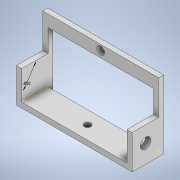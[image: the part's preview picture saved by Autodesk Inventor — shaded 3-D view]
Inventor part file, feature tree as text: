
AUTODESK INVENTOR PART (.ipt)
format: ipt  version: 2021.2 (Build 252289000, 289)  size: 291,328 bytes
history: native  units: in
note: dims shown in document units (in); Inventor stores cm internally (conversion verified against a paired STEP export)
features: sketch x28, extrude x21
ambient origin geometry x8: Origin, YZ Plane, XZ Plane, XY Plane, X Axis, Y Axis, Z Axis, Center Point
bodies: Solid1 (feature_tree)
feature tree (49):
  extrude  "Extrusion1"  Depth=4.0in
  extrude  "Extrusion2"  Depth=0.2in
  sketch  "Sketch3"  dims[d4=0.2in d5=0.2in]
  extrude  "Extrusion3"  Depth=0.2in
  extrude  "Extrusion4"  Depth=2.0in
  sketch  "Sketch7"  dims[d11=0.1875in d12=0.0in d13=0.125in d14=0.0in]
  extrude  "Extrusion6"  Depth=0.2in
  sketch  "Sketch9"  dims[d21=0.3in d22=0.0in d23=0.0125in d24=0.0in]
  extrude  "Extrusion7"  Depth=0.125in TaperAngle=0.0deg
  sketch  "Sketch10"  dims[d25=0.2in d26=2.0in d27=0.0in]
  sketch  "Sketch11"  dims[d28=0.2in d29=2.0in d30=0.0in]
  extrude  "Extrusion8"  Depth=0.4in
  extrude  "Extrusion9"  Depth=0.0125in TaperAngle=0.0deg
  extrude  "Extrusion10"  Depth=2.0in TaperAngle=0.0deg
  extrude  "Extrusion11"  Depth=2.0in TaperAngle=0.0deg
  extrude  "Extrusion12"  Depth=0.188in TaperAngle=0.0deg
  sketch  "Sketch17"  dims[d48=0.4in d49=0.5in d50=0.0in]
  sketch  "Sketch18"  dims[d51=0.5in d52=0.0in d53=4.0in]
  extrude  "Extrusion13"  Depth=0.188in
  extrude  "Extrusion14"  Depth=0.3755in TaperAngle=0.0deg
  extrude  "Extrusion15"  Depth=0.5in TaperAngle=0.0deg
  extrude  "Extrusion16"  Depth=0.5in TaperAngle=0.0deg
  extrude  "Extrusion17"  Depth=0.5in TaperAngle=0.0deg
  extrude  "Extrusion18"  Depth=4.0in
  extrude  "Extrusion19"  Depth=0.5in TaperAngle=0.0deg
  extrude  "Extrusion20"  Depth=0.3in
  extrude  "Extrusion21"  Depth=0.4in TaperAngle=0.0deg
  sketch  "Sketch28"
  extrude  "Extrusion22"  [1 undecoded]
  sketch  "Sketch1"  dims[d0=1.0in d1=4.0in]
  sketch  "Sketch2"  dims[d2=1.0in d3=0.2in]
  sketch  "Sketch4"  dims[d6=1.0in d7=0.0in d8=2.0in]
  sketch  "Sketch5"  dims[d9=0.2in d10=0.2in]
  sketch  "Sketch8"  dims[d15=0.1875in d16=0.0in d20=0.4in]
  sketch  "Sketch12"  dims[d31=1.0in d32=0.0in d33=0.188in d34=0.0in]
  sketch  "Sketch13"  dims[d35=0.188in d36=0.0in d37=0.85in]
  sketch  "Sketch14"  dims[d38=0.25in d39=0.3755in d40=0.0in]
  sketch  "Sketch15"  dims[d41=0.5in d42=0.0in d43=0.5in d44=0.0in]
  sketch  "Sketch16"  dims[d45=0.4in d46=0.5in d47=0.0in]
  sketch  "Sketch19"  dims[d54=0.3in d55=0.5in d56=0.0in]
  sketch  "Sketch20"  dims[d57=0.4in d58=0.0in d60=0.3in]
  sketch  "Sketch21"  dims[d61=0.4in d62=0.0in d63=0.4in d64=0.0in]
  sketch  "Sketch22"
  sketch  "Sketch23"
  sketch  "Sketch24"
  sketch  "Sketch25"
  sketch  "Sketch26"
  sketch  "Sketch27"
  sketch  "Sketch29"
note: 1 required parameter value undecoded (feature->parameter linkage not recoverable at this tier; creation-order binding heuristic only, values carry confidence <= 0.55)
